# Revit family: 1Electronics_Community_Biamp_Voice-Range-Horn-System_RMG-200A
name_source: partatom
category: Communication Devices
units: mm (PartAtom-declared; Revit-internal decimal feet)

## family parameters
Cut with Voids When Loaded = No
Host = Face
Maintain Annotation Orientation = No
OmniClass Number = 23.85.10.11.14.14.14
Part Type = Normal
Room Calculation Point = No
Round Connector Dimension = Use Diameter
Shared = No

## types (2) — shared parameters
Axial Q / DI = 35 / 15.4, 2 kHz to 4 kHz
Crossover Frequency = No internal crossover
Default Elevation = 48 "
Depth = 25 "
Description = RMG-200A Voice-Range Horn System with Swivel Yoke Bracket
Drivers = MF 1 x M200, Ferrofluid-cooled
Enclosure = Fiberglass
Environmental Performance = IEC529 IP66W rating with a minimum 5-degree downward aiming angle
Height = 9.76 "
Housing Material = Biamp - Metal - Silver
Loudspeaker Type = Voice-range horn system
Manufacturer = Biamp
Mounting/Rigging Provisions = (4) 1/4 holes at the corners of the horn mouth
Optional Accessories = System controller
Product Documentation Link = https://downloads.biamp.com
Product Page URL = https://www.biamp.com
Product data url = https://bimobject.com
Recommended Signal Processing = 400 Hz high pass filter 24dB / Oct.
Required Accessories = 400 Hz high pass filter 24dB / Oct.
Supplied Accessories = Swivel yoke bracket
URL = https://www.biamp.com
Width = 17.64 "

## per-type parameters (varying)
| type | Connector Description | Input Connection | Max Input Ratings | Maximum Output | Minimum Impedance | Nominal Impedance | Nominal –6dB Beamwidth | Operating Range | Recommended Power Amplifier | Sensitivity (1W/1m) | Shipping Weight | Weight |
| RMG-200A | Terminal strip; 75W continuous, 120W program | 16 gauge, 2 conductor, 12 foot (4 m) SJOW cable through gland nut | 75W continuous, 120W program | 134 dB SPL / 141 dB SPL (peak) | 10.8 Ohms @ 1.8 kHz | 11 Ohms | 50°H (+14° / -9°, 2 kHz to 4 kHz);40°V (+10° / -10°, 2 kHz to 4 kHz) | 400 Hz to 8 Khz;500 Hz to 4 khz (±3.5 dB) | 100W to 140W | 115 dB SPL (400 Hz to 4 kHz 1/3 octave bands) | 27.00 lb | 21.00 lb |
| RMG-200AT | Terminal strip; 75 / 38 / 19 / 9 W autoformer taps 70V | 18 gauge, 5 conductor, 12 foot SJOW cable through gland nut | 75 / 38 / 19 / 9 watt autoformer taps @ 70v | 133 dB SPL / 140 dB SPL (peak) | 70.5 ohms @ 1.8 kHz (75W tap @ 70V) | 72 ohms (75W tap @ 70V) | 50°H (+-4° / -9°, 2 kHz to 4 kHz);40°V (+10° / -10°, 2 kHz to 4 kHz) | 400 Hz to 8 Khz;500 Hz to 4 kHz (±3 dB) |  | 114 dB SPL (400 Hz to 4 kHz 1/3 octave bands) | 30.00 lb | 24.30 lb |

note: column(s) folded — value = type name in every type: Model

## geometry (parser evidence)
native form markers: Sweep x5
no freeform markers — native parametric forms only
